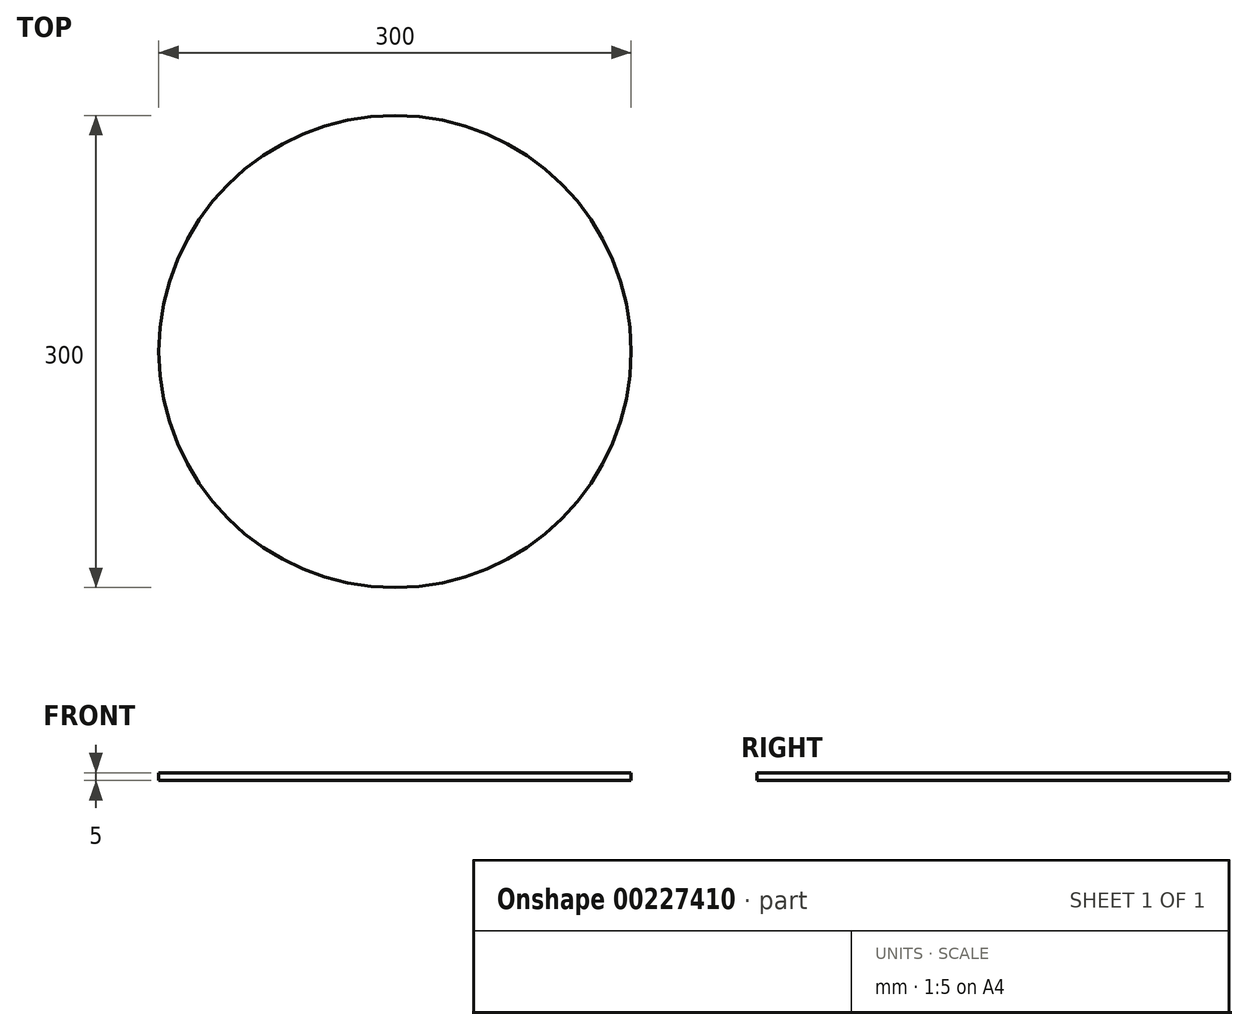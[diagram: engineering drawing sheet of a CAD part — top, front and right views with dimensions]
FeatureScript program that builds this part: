
annotation { "Feature Type Name" : "Feature", "Feature Type Description" : "" }
export const myFeature = defineFeature(function(context is Context, id is Id, definition is map)
    precondition{}
    {
        {
            var Q0;
            Q0=qCreatedBy(makeId("Top.planeOp"),FACE);
            var sketch = newSketch(context, id + "F0", { "sketchPlane" : qUnion([Q0])});
            skCircle(sketch, "E0", {"center": v(0, 0) * mm, "radius": 150 * mm});
            skSolve(sketch);
        }
        {
            var Q0;
            Q0 = qSketchRegion(id + "F0", true);
            extrude(context, id + "F1", {"entities" : qUnion([Q0]), "depth" : 5 * mm});
        }
    });
